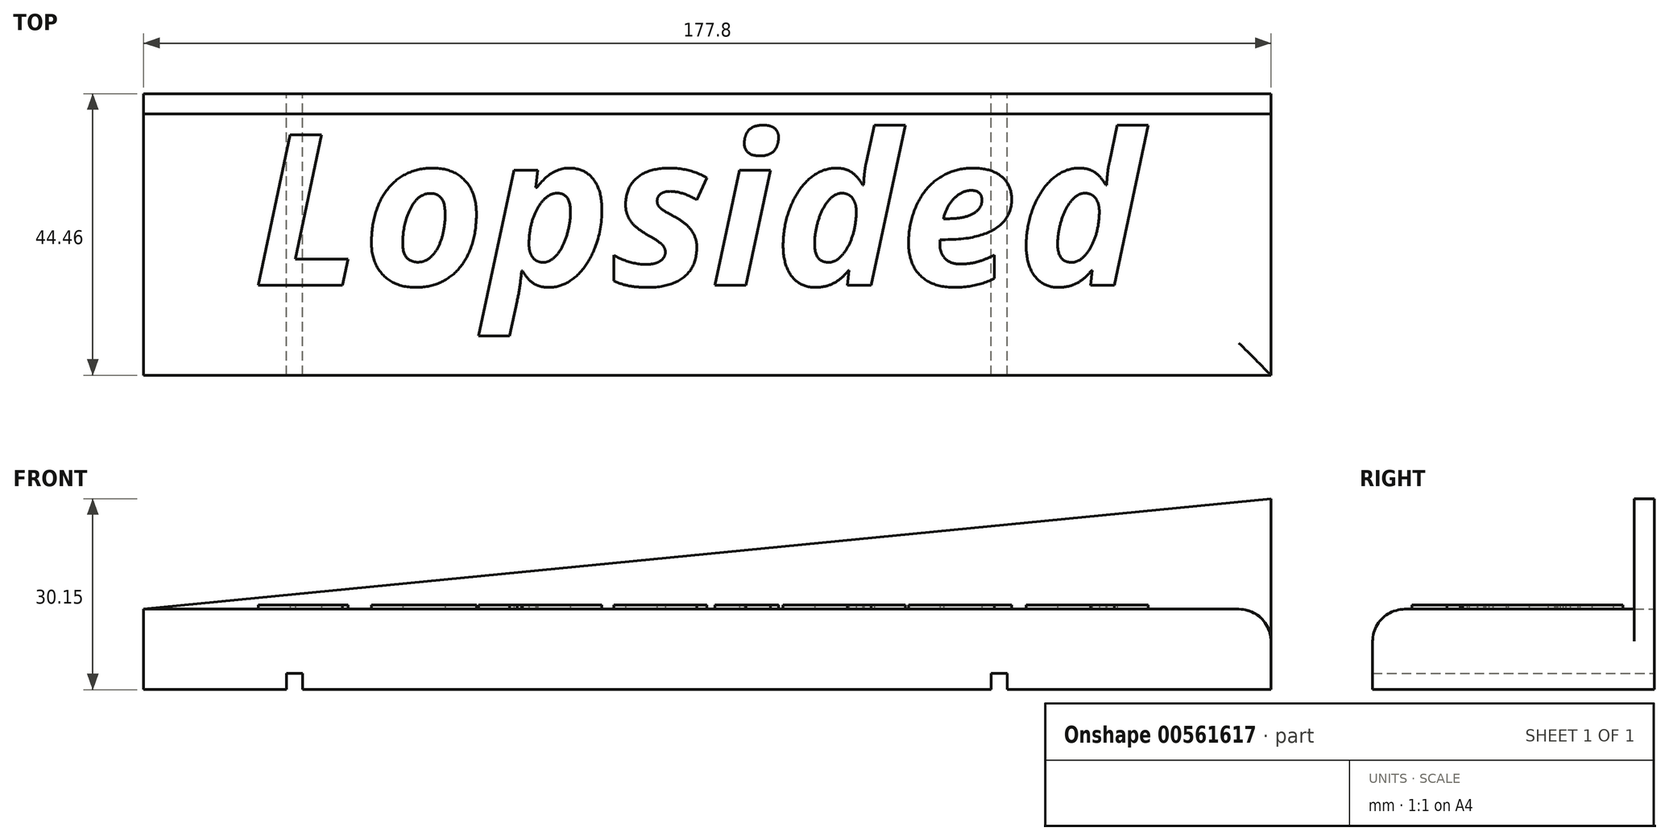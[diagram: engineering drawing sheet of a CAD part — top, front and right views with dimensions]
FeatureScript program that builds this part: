
annotation { "Feature Type Name" : "Feature", "Feature Type Description" : "" }
export const myFeature = defineFeature(function(context is Context, id is Id, definition is map)
    precondition{}
    {
        {
            var Q0;
            Q0=qCreatedBy(makeId("Front.planeOp"),FACE);
            var sketch = newSketch(context, id + "F0", { "sketchPlane" : qUnion([Q0])});
            skLineSegment(sketch, "E0.bottom", {"start": v(-88.9, -15.88) * mm, "end": v(88.9, -15.88) * mm});
            skLineSegment(sketch, "E0.top", {"start": v(-88.9, 15.88) * mm, "end": v(88.9, 15.88) * mm});
            skLineSegment(sketch, "E0.left", {"start": v(-88.9, -15.88) * mm, "end": v(-88.9, 15.88) * mm});
            skLineSegment(sketch, "E0.right", {"start": v(88.9, -15.88) * mm, "end": v(88.9, 15.88) * mm});
            skLineSegment(sketch, "E1", {"start": v(-88.9, 15.88) * mm, "end": v(88.9, -15.88) * mm, "construction": true});
            skPoint(sketch, "E2", {"position": v(0, 0) * mm});
            skSolve(sketch);
        }
        {
            var Q0;
            Q0=makeQuery(id+"F0.imprint","IMPRINT",FACE,{"disambiguationData":[TD([[makeQuery(id+"F0.imprint","IMPRINT",EDGE,{"derivedFrom":sQuery(id+"F0.wireOp",EDGE,"E0.bottom")}),1.0]])]});
            extrude(context, id + "F10", {"entities" : qUnion([Q0]), "endBound" : BoundingType.SYMMETRIC, "depth" : 44.45 * mm});
        }
        {
            var Q0;
            Q0=qCreatedBy(makeId("Front.planeOp"),FACE);
            var sketch = newSketch(context, id + "F1", { "sketchPlane" : qUnion([Q0])});
            skLineSegment(sketch, "E3.0", {"start": v(-88.9, -15.88) * mm, "end": v(88.9, -15.88) * mm, "construction": true});
            skLineSegment(sketch, "E4.bottom", {"start": v(-66.36, -15.88) * mm, "end": v(-63.82, -15.88) * mm});
            skLineSegment(sketch, "E4.top", {"start": v(-66.36, -13.34) * mm, "end": v(-63.82, -13.34) * mm});
            skLineSegment(sketch, "E4.left", {"start": v(-66.36, -15.88) * mm, "end": v(-66.36, -13.34) * mm});
            skLineSegment(sketch, "E4.right", {"start": v(-63.82, -15.88) * mm, "end": v(-63.82, -13.34) * mm});
            skLineSegment(sketch, "E5.bottom", {"start": v(44.77, -15.88) * mm, "end": v(47.3, -15.88) * mm});
            skLineSegment(sketch, "E5.top", {"start": v(44.77, -13.34) * mm, "end": v(47.3, -13.34) * mm});
            skLineSegment(sketch, "E5.left", {"start": v(44.77, -15.88) * mm, "end": v(44.77, -13.34) * mm});
            skLineSegment(sketch, "E5.right", {"start": v(47.3, -15.88) * mm, "end": v(47.3, -13.34) * mm});
            skPoint(sketch, "E6", {"position": v(-65.09, -15.88) * mm});
            skPoint(sketch, "E7", {"position": v(46.04, -15.88) * mm});
            skSolve(sketch);
        }
        {
            var Q0;
            Q0=qSketchRegion(id+"F1",true);
            extrude(context, id + "F2", {"entities" : qUnion([Q0]), "operationType" : NewBodyOperationType.REMOVE, "endBound" : BoundingType.UP_TO_NEXT, "depth" : 50.8 * mm, "hasSecondDirection" : true, "secondDirectionBound" : SecondDirectionBoundingType.UP_TO_NEXT, "secondDirectionOppositeDirection" : true, "secondDirectionDepth" : 25.4 * mm});
        }
        {
            var Q0;
            Q0=makeQuery(id+"F10.opExtrude","SWEPT_FACE",FACE,{"disambiguationData":[OSD([sQuery(id+"F0.wireOp",EDGE,"E0.top")])]});
            var sketch = newSketch(context, id + "F3", { "sketchPlane" : qUnion([Q0])});
            skLineSegment(sketch, "E8.bottom", {"start": v(-95.25, 19.05) * mm, "end": v(95.25, 19.05) * mm});
            skLineSegment(sketch, "E8.top", {"start": v(-95.25, -25.4) * mm, "end": v(95.25, -25.4) * mm});
            skLineSegment(sketch, "E8.left", {"start": v(-95.25, 19.05) * mm, "end": v(-95.25, -25.4) * mm});
            skLineSegment(sketch, "E8.right", {"start": v(95.25, 19.05) * mm, "end": v(95.25, -25.4) * mm});
            skSolve(sketch);
        }
        {
            var Q0;
            Q0 = qSketchRegion(id + "F3", true);
            extrude(context, id + "F4", {"entities" : qUnion([Q0]), "operationType" : NewBodyOperationType.REMOVE, "endBound" : BoundingType.SYMMETRIC, "depth" : 38.1 * mm, "offsetDistance" : 25.4 * mm});
        }
        {
            var Q0;
            Q0=makeQuery(id+"F4.boolean.opBoolean","COPY",FACE,{"derivedFrom":makeQuery(id+"F4.opExtrude","SWEPT_FACE",FACE,{"disambiguationData":[OSD([sQuery(id+"F3.wireOp",EDGE,"E8.bottom")])]})});
            var sketch = newSketch(context, id + "F5", { "sketchPlane" : qUnion([Q0])});
            skLineSegment(sketch, "E9", {"start": v(-88.9, -3.18) * mm, "end": v(88.9, 14.27) * mm});
            skLineSegment(sketch, "E10", {"start": v(88.9, 14.27) * mm, "end": v(92.26, 24.14) * mm});
            skLineSegment(sketch, "E11", {"start": v(92.26, 24.14) * mm, "end": v(-88.9, 22.2) * mm});
            skLineSegment(sketch, "E12", {"start": v(-88.9, 22.2) * mm, "end": v(-88.9, -3.17) * mm});
            skSolve(sketch);
        }
        {
            var Q0;
            Q0 = qSketchRegion(id + "F5", true);
            extrude(context, id + "F6", {"entities" : qUnion([Q0]), "operationType" : NewBodyOperationType.REMOVE, "endBound" : BoundingType.SYMMETRIC, "depth" : 76.2 * mm, "offsetDistance" : 25.4 * mm});
        }
        {
            var Q0;
            Q0=makeQuery(id+"F6.boolean.opBoolean","COPY",EDGE,{"derivedFrom":makeQuery(id+"F6.opExtrude","SWEPT_EDGE",EDGE,{"disambiguationData":[OSD([sQuery(id+"F3.wireOp",EDGE,"E8.bottom"),sQuery(id+"F5.wireOp",EDGE,"E9"),sQuery(id+"F5.wireOp",EDGE,"E12")])]})});
            var Q1;
            Q1=makeQuery(id+"F4.boolean.opBoolean","INTERSECT",EDGE,{"derivedFrom":[makeQuery(id+"F10.opExtrude","CAP_FACE",FACE,{"disambiguationData":[OSD([sQuery(id+"F0.wireOp",EDGE,"E0.bottom"),sQuery(id+"F0.wireOp",EDGE,"E0.top"),sQuery(id+"F0.wireOp",EDGE,"E0.left"),sQuery(id+"F0.wireOp",EDGE,"E0.right")])],"isStart":false}),makeQuery(id+"F4.opExtrude","CAP_FACE",FACE,{"disambiguationData":[OSD([sQuery(id+"F3.wireOp",EDGE,"E8.bottom"),sQuery(id+"F3.wireOp",EDGE,"E8.top"),sQuery(id+"F3.wireOp",EDGE,"E8.left"),sQuery(id+"F3.wireOp",EDGE,"E8.right")])],"isStart":true})]});
            var Q2;
            Q2=makeQuery(id+"F4.boolean.opBoolean","INTERSECT",EDGE,{"derivedFrom":[makeQuery(id+"F10.opExtrude","SWEPT_FACE",FACE,{"disambiguationData":[OSD([sQuery(id+"F0.wireOp",EDGE,"E0.right")])]}),makeQuery(id+"F4.opExtrude","CAP_FACE",FACE,{"disambiguationData":[OSD([sQuery(id+"F3.wireOp",EDGE,"E8.bottom"),sQuery(id+"F3.wireOp",EDGE,"E8.top"),sQuery(id+"F3.wireOp",EDGE,"E8.left"),sQuery(id+"F3.wireOp",EDGE,"E8.right")])],"isStart":true})]});
            var Q3;
            Q3=makeQuery(id+"F6.boolean.opBoolean","COPY",EDGE,{"derivedFrom":makeQuery(id+"F6.opExtrude","SWEPT_EDGE",EDGE,{"disambiguationData":[OSD([sQuery(id+"F0.wireOp",EDGE,"E0.right"),sQuery(id+"F3.wireOp",EDGE,"E8.bottom"),sQuery(id+"F5.wireOp",EDGE,"E9"),sQuery(id+"F5.wireOp",EDGE,"E10")])]})});
            fillet(context, id + "F7", {"entities" : qUnion([Q0, Q1, Q2, Q3]), "radius" : 5.08 * mm, "tangentPropagation" : true, "allowEdgeOverflow" : false});
        }
        {
            var Q0;
            Q0=makeQuery(id+"F4.boolean.opBoolean","COPY",FACE,{"derivedFrom":makeQuery(id+"F4.opExtrude","CAP_FACE",FACE,{"disambiguationData":[OSD([sQuery(id+"F3.wireOp",EDGE,"E8.bottom"),sQuery(id+"F3.wireOp",EDGE,"E8.top"),sQuery(id+"F3.wireOp",EDGE,"E8.left"),sQuery(id+"F3.wireOp",EDGE,"E8.right")])],"isStart":true})});
            var sketch = newSketch(context, id + "F8", { "sketchPlane" : qUnion([Q0])});
            skText(sketch, "E13", { "text": "Lopsided", "fontName": "OpenSans-BoldItalic.ttf"});
            const initialGuessF8  = {"E13": [-0.07168, -0.00804, 1, 0, 0.02397]};
            skSetInitialGuess(sketch, initialGuessF8);
            skSolve(sketch);
        }
        {
            var Q0;
            Q0 = qSketchRegion(id + "F8", true);
            extrude(context, id + "F9", {"entities" : qUnion([Q0]), "operationType" : NewBodyOperationType.ADD, "depth" : 0.64 * mm, "offsetDistance" : 25.4 * mm});
        }
    });
